# Revit family: FantiniCosmi_BIM_C68
name_source: partatom
category: Generic Models
units: mm (PartAtom-declared; Revit-internal decimal feet)

## family parameters
Always vertical = Yes
Can host rebar = No
Cut with Voids When Loaded = No
Part Type = Normal
Room Calculation Point = No
Round Connector Dimension = Use Diameter
Shared = No
Work Plane-Based = No

## types (1)
- Standard
    Body admissible temperature = 45 °C
    Catalog web link = https://www.fantinicosmi.it
    Color = White
    Comfort temperature range = 16 ÷ 34 °C
    Default Elevation = 0 mm  [stored 0 ft]
    Description = Electronic room thermostat with batteries, 3 temperature levels
    Differential = 0,25 K
    Economy temperature range = 5 ÷ 23 °C
    Part Number = C68
    Power supply = 2 batteries AA 1.5 V
    Type of action (Micro disconnection) = 1B

note: [stored X ft] marks values corroborated as IEEE doubles in the binary element streams (Revit-internal decimal feet)

## geometry (parser evidence)
native form markers: Sweep x3
no freeform markers — native parametric forms only
